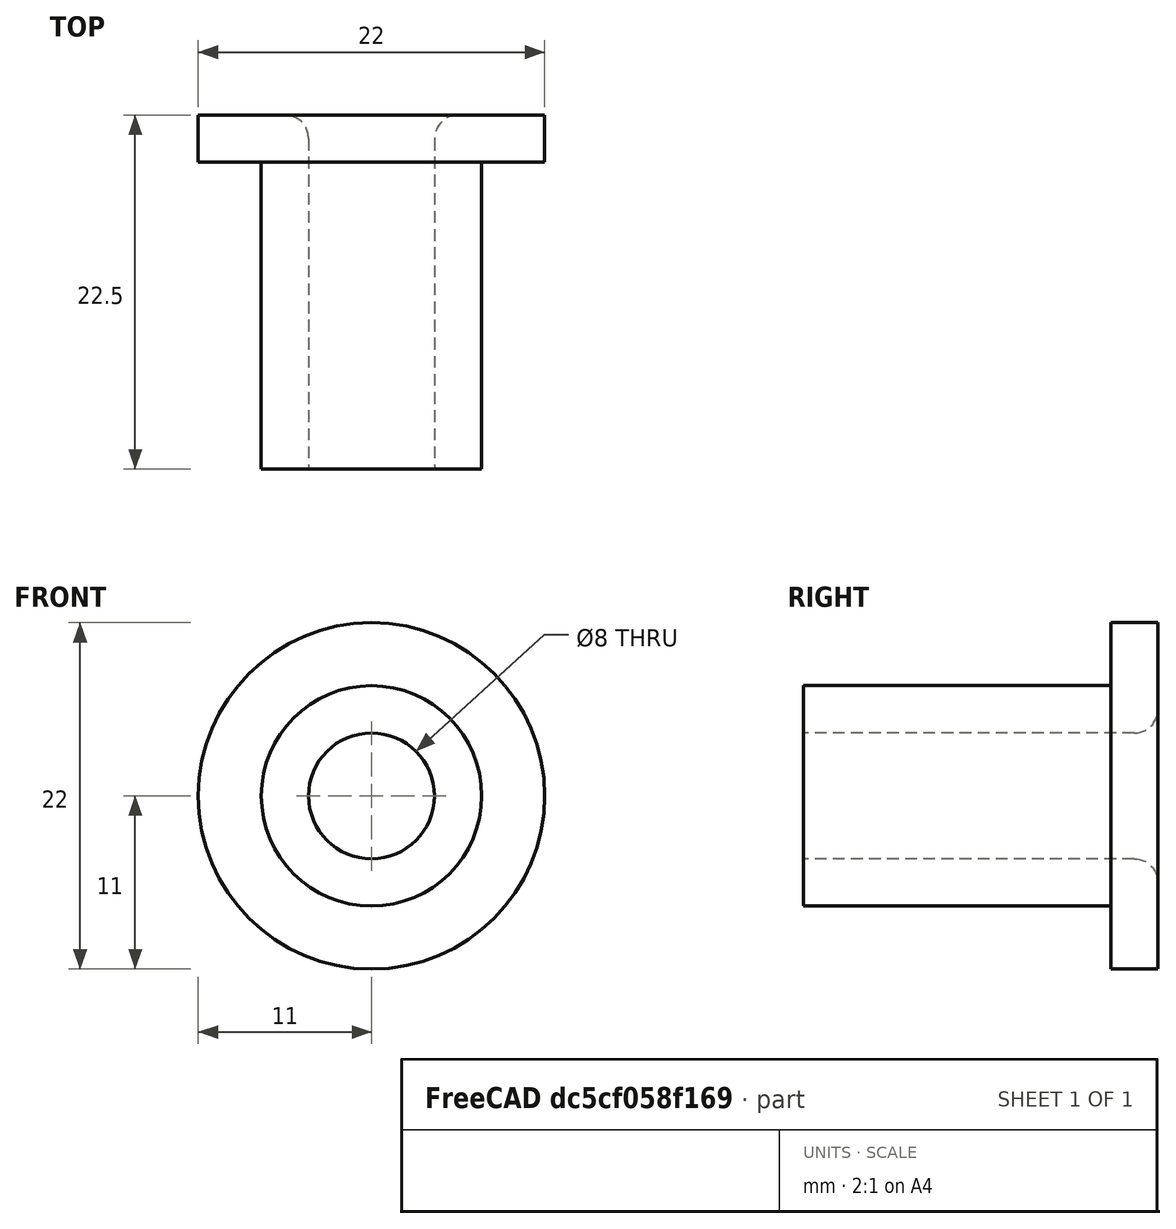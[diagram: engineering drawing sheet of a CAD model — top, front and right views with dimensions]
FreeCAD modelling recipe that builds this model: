
FCSTD DOCUMENT  (FreeCAD 0.15R4671 (Git))
Label: separator
License: All rights reserved
LicenseURL: http://en.wikipedia.org/wiki/All_rights_reserved
objects: Sketcher::SketchObject×1, PartDesign::Revolution×1
note: 3 computed .brp shape members not serialized (recipe doc carries the construction recipe); baked Part::Feature solids carry a one-line shape summary decoded from their .brp

FEATURE [Sketcher::SketchObject] Sketch
  sketch-geometry (8):
    g0: LineSegment StartX=4 StartY=9.75 StartZ=0 EndX=4 EndY=-11.25 EndZ=0
    g1: LineSegment StartX=4 StartY=-11.25 StartZ=0 EndX=7 EndY=-11.25 EndZ=0
    g2: LineSegment StartX=7 StartY=-11.25 StartZ=0 EndX=7 EndY=8.25 EndZ=0
    g3: LineSegment StartX=7 StartY=8.25 StartZ=0 EndX=11 EndY=8.25 EndZ=0
    g4: LineSegment StartX=11 StartY=8.25 StartZ=0 EndX=11 EndY=11.25 EndZ=0
    g5: LineSegment StartX=7 StartY=11.25 StartZ=0 EndX=5.5 EndY=11.25 EndZ=0
    g6: ArcOfCircle CenterX=5.5 CenterY=9.75 CenterZ=0 NormalX=0 NormalY=0 NormalZ=1 Radius=1.5 StartAngle=1.5708 EndAngle=3.14159
    g7: LineSegment StartX=11 StartY=11.25 StartZ=0 EndX=7 EndY=11.25 EndZ=0
  constraints (22):
    c: Vertical(g0)
    c: Horizontal(g1)
    c: DistanceX(g3) = 4
    c: DistanceY(g5,g3) = -3
    c: Tangent(g5,g6) = -1.5708
    c: Tangent(g0,g6) = -1.5708
    c: DistanceY(g2,g0) = 1.5
    c: DistanceX(g-1,g0) = 4
    c: DistanceX(g0,g2) = 3
    c: Symmetric(g1,g5,g-1)
    c: Horizontal(g5)
    c: Horizontal(g3)
    c: Vertical(g2)
    c: Vertical(g4)
    c: Coincident(g3,g2)
    c: Coincident(g4,g3)
    c: DistanceY(g5,g1) = -22.5
    c: Coincident(g1,g2)
    c: Coincident(g7,g4)
    c: Coincident(g7,g5)
    c: Horizontal(g7)
    c: Coincident(g1,g0)
FEATURE [PartDesign::Revolution] Revolution  label="separator"
  Angle = 360
  Axis = (0,1,0)
  Base = (0,0,0)
  ReferenceAxis = -> Sketch [V_Axis]
  Reversed = true
  Sketch = -> Sketch
